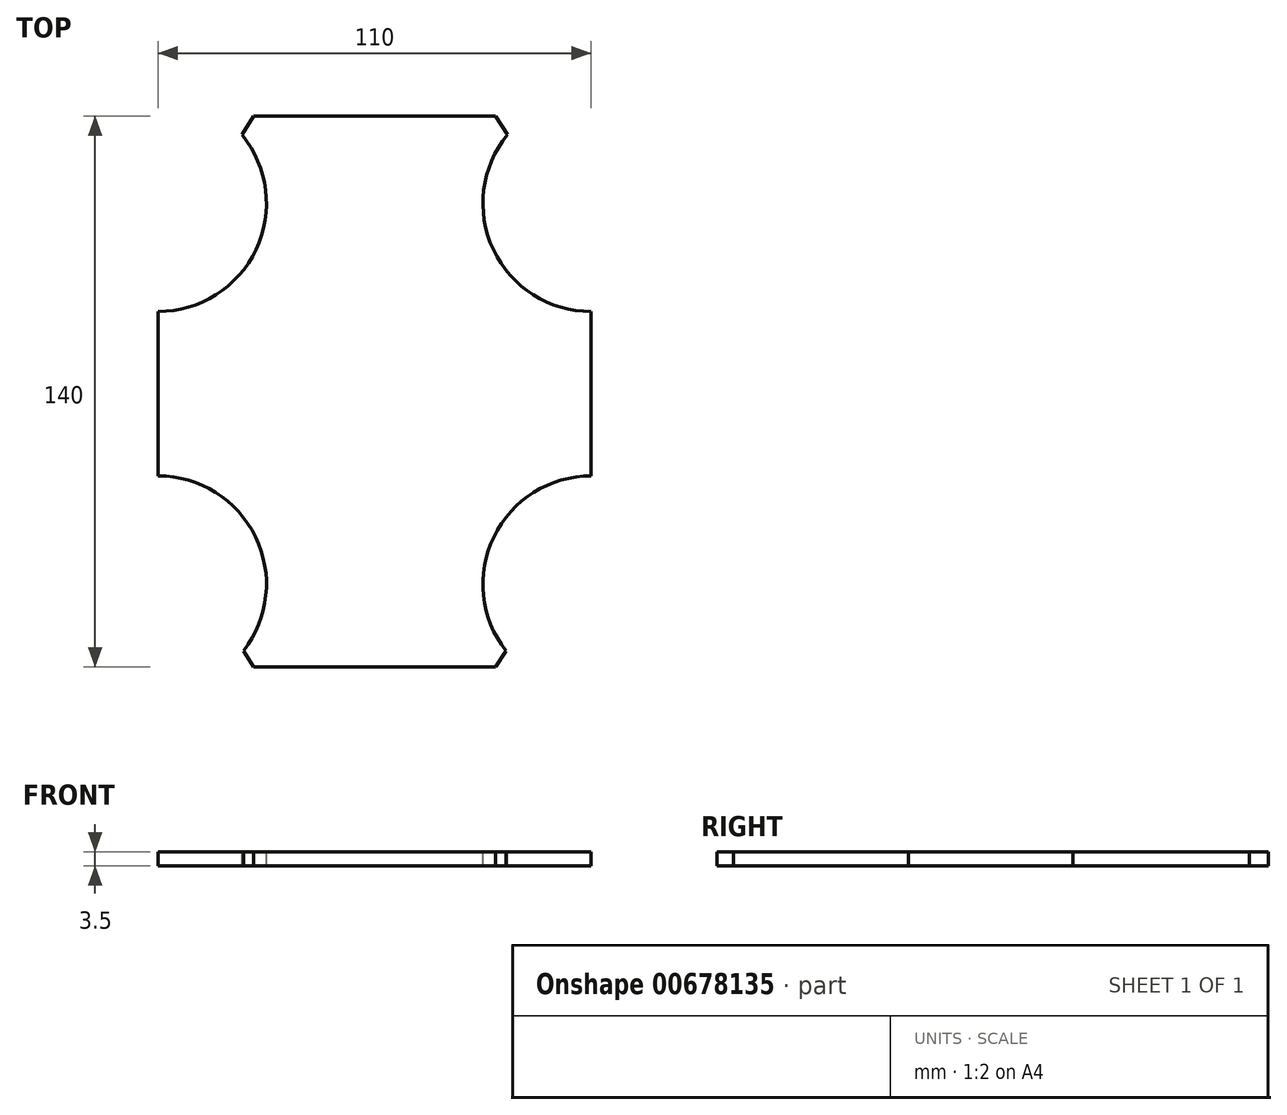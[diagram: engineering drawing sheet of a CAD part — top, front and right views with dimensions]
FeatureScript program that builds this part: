
annotation { "Feature Type Name" : "Feature", "Feature Type Description" : "" }
export const myFeature = defineFeature(function(context is Context, id is Id, definition is map)
    precondition{}
    {
        {
            var Q0;
            Q0=qCreatedBy(makeId("Top.planeOp"),FACE);
            var sketch = newSketch(context, id + "F0", { "sketchPlane" : qUnion([Q0])});
            skLineSegment(sketch, "E0.bottom", {"start": v(-55, 70) * mm, "end": v(55, 70) * mm});
            skLineSegment(sketch, "E0.top", {"start": v(-55, -70) * mm, "end": v(55, -70) * mm});
            skLineSegment(sketch, "E0.left", {"start": v(-55, 70) * mm, "end": v(-55, -70) * mm});
            skLineSegment(sketch, "E0.right", {"start": v(55, 70) * mm, "end": v(55, -70) * mm});
            skSolve(sketch);
        }
        {
            var Q0;
            Q0=makeQuery(id+"F0.imprint","IMPRINT",FACE,{"disambiguationData":[TD([[makeQuery(id+"F0.imprint","IMPRINT",EDGE,{"derivedFrom":sQuery(id+"F0.wireOp",EDGE,"E0.bottom")}),-1.0]])]});
            extrude(context, id + "F1", {"entities" : qUnion([Q0]), "depth" : 3.5 * mm, "offsetDistance" : 25 * mm});
        }
        {
            var Q0;
            Q0=makeQuery(id+"F1.opExtrude","CAP_FACE",FACE,{"disambiguationData":[OSD([sQuery(id+"F0.wireOp",EDGE,"E0.bottom"),sQuery(id+"F0.wireOp",EDGE,"E0.top"),sQuery(id+"F0.wireOp",EDGE,"E0.left"),sQuery(id+"F0.wireOp",EDGE,"E0.right")])],"isStart":false});
            var sketch = newSketch(context, id + "F2", { "sketchPlane" : qUnion([Q0])});
            skCircle(sketch, "E1", {"center": v(-55, 47.83) * mm, "radius": 27.5 * mm});
            skCircle(sketch, "E2", {"center": v(55, 47.83) * mm, "radius": 27.5 * mm});
            skCircle(sketch, "E3", {"center": v(-55, -48.94) * mm, "radius": 27.5 * mm});
            skCircle(sketch, "E4", {"center": v(55, -48.94) * mm, "radius": 27.5 * mm});
            skSolve(sketch);
        }
        {
            var Q0;
            {var subQ0=sQuery(id+"F2.wireOp",EDGE,"E1");var subQ1=makeQuery(id+"F1.opExtrude","CAP_EDGE",EDGE,{"disambiguationData":[OSD([sQuery(id+"F0.wireOp",EDGE,"E0.bottom")])],"isStart":false});var subQ2=makeQuery(id+"F2.imprint","INTERSECT",VERTEX,{"derivedFrom":[subQ1,subQ0]});Q0=makeQuery(id+"F2.imprint","IMPRINT",FACE,{"disambiguationData":[TD([[makeQuery(id+"F2.imprint","IMPRINT",EDGE,{"disambiguationData":[TD([[subQ2,-1.0]])],"derivedFrom":subQ0}),1.0]])]});}
            var Q1;
            {var subQ0=sQuery(id+"F2.wireOp",EDGE,"E1");var subQ1=makeQuery(id+"F1.opExtrude","CAP_EDGE",EDGE,{"disambiguationData":[OSD([sQuery(id+"F0.wireOp",EDGE,"E0.bottom")])],"isStart":false});var subQ2=makeQuery(id+"F2.imprint","INTERSECT",VERTEX,{"derivedFrom":[subQ1,subQ0]});Q1=makeQuery(id+"F2.imprint","IMPRINT",FACE,{"disambiguationData":[TD([[makeQuery(id+"F2.imprint","IMPRINT",EDGE,{"disambiguationData":[TD([[subQ2,1.0]])],"derivedFrom":subQ0}),1.0]])]});}
            var Q2;
            {var subQ0=sQuery(id+"F2.wireOp",EDGE,"E3");var subQ1=makeQuery(id+"F1.opExtrude","CAP_EDGE",EDGE,{"disambiguationData":[OSD([sQuery(id+"F0.wireOp",EDGE,"E0.left")])],"isStart":false});var subQ2=makeQuery(id+"F2.imprint","INTERSECT",VERTEX,{"disambiguationData":[OD(0.0)],"derivedFrom":[subQ1,subQ0]});Q2=makeQuery(id+"F2.imprint","IMPRINT",FACE,{"disambiguationData":[TD([[makeQuery(id+"F2.imprint","IMPRINT",EDGE,{"disambiguationData":[TD([[subQ2,-1.0]])],"derivedFrom":subQ0}),1.0]])]});}
            var Q3;
            {var subQ0=sQuery(id+"F2.wireOp",EDGE,"E3");var subQ1=makeQuery(id+"F1.opExtrude","CAP_EDGE",EDGE,{"disambiguationData":[OSD([sQuery(id+"F0.wireOp",EDGE,"E0.left")])],"isStart":false});var subQ2=makeQuery(id+"F2.imprint","INTERSECT",VERTEX,{"disambiguationData":[OD(0.0)],"derivedFrom":[subQ1,subQ0]});Q3=makeQuery(id+"F2.imprint","IMPRINT",FACE,{"disambiguationData":[TD([[makeQuery(id+"F2.imprint","IMPRINT",EDGE,{"disambiguationData":[TD([[subQ2,1.0]])],"derivedFrom":subQ0}),1.0]])]});}
            var Q4;
            {var subQ0=sQuery(id+"F2.wireOp",EDGE,"E2");var subQ1=makeQuery(id+"F1.opExtrude","CAP_EDGE",EDGE,{"disambiguationData":[OSD([sQuery(id+"F0.wireOp",EDGE,"E0.bottom")])],"isStart":false});var subQ2=makeQuery(id+"F2.imprint","INTERSECT",VERTEX,{"derivedFrom":[subQ1,subQ0]});Q4=makeQuery(id+"F2.imprint","IMPRINT",FACE,{"disambiguationData":[TD([[makeQuery(id+"F2.imprint","IMPRINT",EDGE,{"disambiguationData":[TD([[subQ2,-1.0]])],"derivedFrom":subQ0}),1.0]])]});}
            var Q5;
            {var subQ0=sQuery(id+"F2.wireOp",EDGE,"E2");var subQ1=makeQuery(id+"F1.opExtrude","CAP_EDGE",EDGE,{"disambiguationData":[OSD([sQuery(id+"F0.wireOp",EDGE,"E0.bottom")])],"isStart":false});var subQ2=makeQuery(id+"F2.imprint","INTERSECT",VERTEX,{"derivedFrom":[subQ1,subQ0]});Q5=makeQuery(id+"F2.imprint","IMPRINT",FACE,{"disambiguationData":[TD([[makeQuery(id+"F2.imprint","IMPRINT",EDGE,{"disambiguationData":[TD([[subQ2,1.0]])],"derivedFrom":subQ0}),1.0]])]});}
            var Q6;
            {var subQ0=sQuery(id+"F2.wireOp",EDGE,"E4");var subQ1=makeQuery(id+"F1.opExtrude","CAP_EDGE",EDGE,{"disambiguationData":[OSD([sQuery(id+"F0.wireOp",EDGE,"E0.right")])],"isStart":false});var subQ2=makeQuery(id+"F2.imprint","INTERSECT",VERTEX,{"disambiguationData":[OD(0.0)],"derivedFrom":[subQ1,subQ0]});Q6=makeQuery(id+"F2.imprint","IMPRINT",FACE,{"disambiguationData":[TD([[makeQuery(id+"F2.imprint","IMPRINT",EDGE,{"disambiguationData":[TD([[subQ2,1.0]])],"derivedFrom":subQ0}),1.0]])]});}
            var Q7;
            {var subQ0=sQuery(id+"F2.wireOp",EDGE,"E4");var subQ1=makeQuery(id+"F1.opExtrude","CAP_EDGE",EDGE,{"disambiguationData":[OSD([sQuery(id+"F0.wireOp",EDGE,"E0.right")])],"isStart":false});var subQ2=makeQuery(id+"F2.imprint","INTERSECT",VERTEX,{"disambiguationData":[OD(0.0)],"derivedFrom":[subQ1,subQ0]});Q7=makeQuery(id+"F2.imprint","IMPRINT",FACE,{"disambiguationData":[TD([[makeQuery(id+"F2.imprint","IMPRINT",EDGE,{"disambiguationData":[TD([[subQ2,-1.0]])],"derivedFrom":subQ0}),1.0]])]});}
            extrude(context, id + "F3", {"entities" : qUnion([Q0, Q1, Q2, Q3, Q4, Q5, Q6, Q7]), "operationType" : NewBodyOperationType.REMOVE, "oppositeDirection" : true, "depth" : 25 * mm, "offsetDistance" : 25 * mm});
        }
        {
            var Q0;
            Q0=makeQuery(id+"F1.opExtrude","CAP_FACE",FACE,{"disambiguationData":[OSD([sQuery(id+"F0.wireOp",EDGE,"E0.bottom"),sQuery(id+"F0.wireOp",EDGE,"E0.top"),sQuery(id+"F0.wireOp",EDGE,"E0.left"),sQuery(id+"F0.wireOp",EDGE,"E0.right")])],"isStart":false});
            var sketch = newSketch(context, id + "F4", { "sketchPlane" : qUnion([Q0])});
            skLineSegment(sketch, "E5", {"start": v(-39.23, 56.51) * mm, "end": v(-26.77, 76.34) * mm});
            skLineSegment(sketch, "E6", {"start": v(-26.77, 76.34) * mm, "end": v(-60.48, 76.34) * mm});
            skLineSegment(sketch, "E7", {"start": v(-60.48, 76.34) * mm, "end": v(-39.23, 56.51) * mm});
            skLineSegment(sketch, "E8.MirrorCS", {"start": v(39.23, 56.51) * mm, "end": v(26.77, 76.34) * mm});
            skLineSegment(sketch, "E9.MirrorCS", {"start": v(26.77, 76.34) * mm, "end": v(60.48, 76.34) * mm});
            skLineSegment(sketch, "E10.MirrorCS", {"start": v(60.48, 76.34) * mm, "end": v(39.23, 56.51) * mm});
            skLineSegment(sketch, "E11.MirrorCS", {"start": v(-60.48, -76.34) * mm, "end": v(-39.23, -56.51) * mm});
            skLineSegment(sketch, "E12.MirrorCS", {"start": v(-26.77, -76.34) * mm, "end": v(-60.48, -76.34) * mm});
            skLineSegment(sketch, "E13.MirrorCS", {"start": v(-39.23, -56.51) * mm, "end": v(-26.77, -76.34) * mm});
            skLineSegment(sketch, "E14.MirrorCS", {"start": v(39.23, -56.51) * mm, "end": v(26.77, -76.34) * mm});
            skLineSegment(sketch, "E15.MirrorCS", {"start": v(26.77, -76.34) * mm, "end": v(60.48, -76.34) * mm});
            skLineSegment(sketch, "E16.MirrorCS", {"start": v(60.48, -76.34) * mm, "end": v(39.23, -56.51) * mm});
            skSolve(sketch);
        }
        {
            var Q0;
            Q0 = qSketchRegion(id + "F4", true);
            extrude(context, id + "F5", {"entities" : qUnion([Q0]), "operationType" : NewBodyOperationType.REMOVE, "oppositeDirection" : true, "depth" : 25 * mm, "offsetDistance" : 25 * mm});
        }
    });
